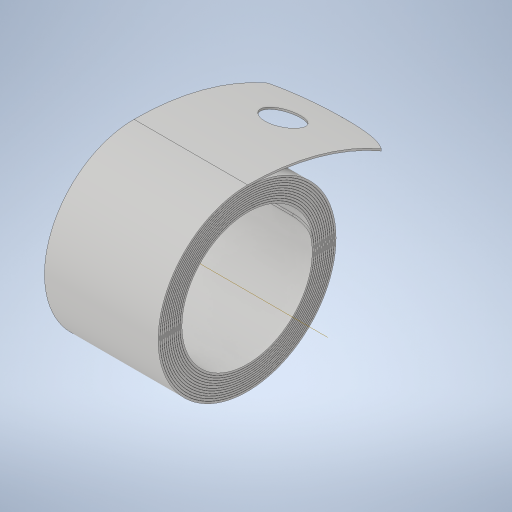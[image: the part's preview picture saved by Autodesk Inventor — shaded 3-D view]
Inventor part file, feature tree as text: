
AUTODESK INVENTOR PART (.ipt)
format: ipt  version: 2023.3 (Build 273359000, 359)  size: 630,784 bytes
history: native  units: in
note: dims shown in document units (in); Inventor stores cm internally (conversion verified against a paired STEP export)
features: other x2, sketch x1
ambient origin geometry x8: Origin, YZ Plane, XZ Plane, XY Plane, X Axis, Y Axis, Z Axis, Center Point
bodies: Solid1 (feature_tree)
feature tree (3):
  sketch  "Sketch1"  dims[d0=1.0041in]
  other  "Work Axis4"
  other  "Cut-Extrude2"
